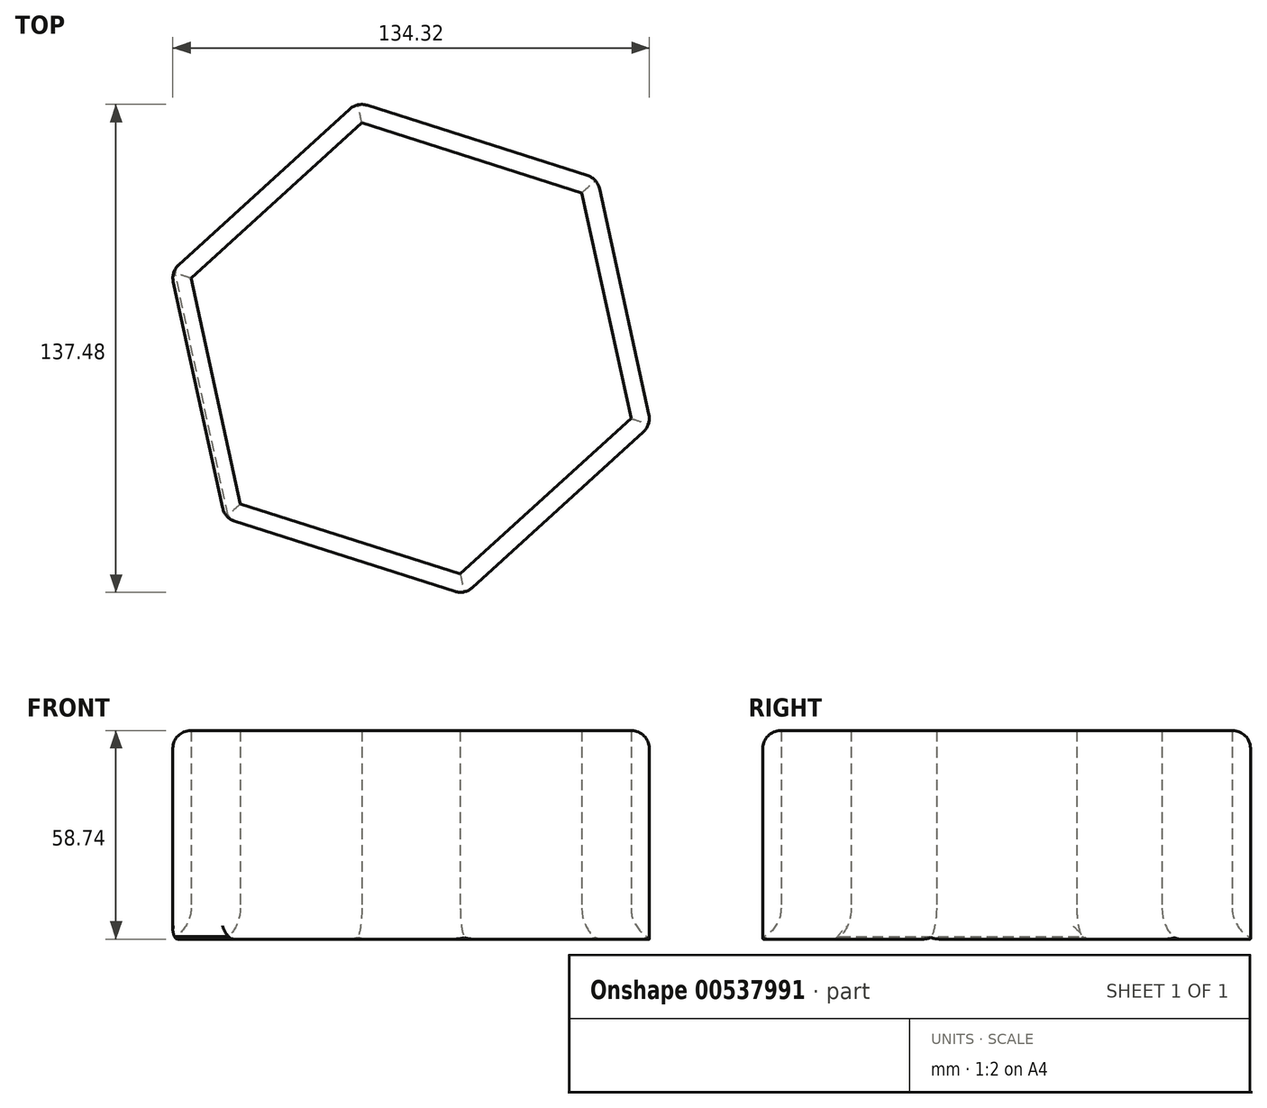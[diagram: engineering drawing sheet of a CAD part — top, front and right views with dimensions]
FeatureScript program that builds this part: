
annotation { "Feature Type Name" : "Feature", "Feature Type Description" : "" }
export const myFeature = defineFeature(function(context is Context, id is Id, definition is map)
    precondition{}
    {
        {
            var Q0;
            Q0=qCreatedBy(makeId("Top.planeOp"),FACE);
            var sketch = newSketch(context, id + "F0", { "sketchPlane" : qUnion([Q0])});
            skCircle(sketch, "E0.cCircle", {"center": v(0, 0) * mm, "radius": 61.5 * mm, "construction": true});
            skLineSegment(sketch, "E0.0", {"start": v(67.66, -21.57) * mm, "end": v(15.15, -69.38) * mm});
            skLineSegment(sketch, "E0.1", {"start": v(15.15, -69.38) * mm, "end": v(-52.51, -47.8) * mm});
            skLineSegment(sketch, "E0.2", {"start": v(-52.51, -47.8) * mm, "end": v(-67.66, 21.57) * mm});
            skLineSegment(sketch, "E0.3", {"start": v(-67.66, 21.57) * mm, "end": v(-15.15, 69.38) * mm});
            skLineSegment(sketch, "E0.4", {"start": v(-15.15, 69.38) * mm, "end": v(52.51, 47.8) * mm});
            skLineSegment(sketch, "E0.5", {"start": v(52.51, 47.8) * mm, "end": v(67.66, -21.57) * mm});
            skPoint(sketch, "E0.0.midPoint", {"position": v(41.4, -45.48) * mm});
            skCircle(sketch, "E1.cCircle", {"center": v(0, 0) * mm, "radius": 56.37 * mm, "construction": true});
            skLineSegment(sketch, "E1.0", {"start": v(62.01, -19.77) * mm, "end": v(13.88, -63.6) * mm});
            skLineSegment(sketch, "E1.1", {"start": v(13.88, -63.6) * mm, "end": v(-48.13, -43.82) * mm});
            skLineSegment(sketch, "E1.2", {"start": v(-48.13, -43.82) * mm, "end": v(-62.01, 19.77) * mm});
            skLineSegment(sketch, "E1.3", {"start": v(-62.01, 19.77) * mm, "end": v(-13.88, 63.6) * mm});
            skLineSegment(sketch, "E1.4", {"start": v(-13.88, 63.6) * mm, "end": v(48.13, 43.82) * mm});
            skLineSegment(sketch, "E1.5", {"start": v(48.13, 43.82) * mm, "end": v(62.01, -19.77) * mm});
            skPoint(sketch, "E1.0.midPoint", {"position": v(37.95, -41.68) * mm});
            skSolve(sketch);
        }
        {
            var Q0;
            Q0 = qSketchRegion(id + "F0", true);
            extrude(context, id + "F1", {"entities" : qUnion([Q0]), "depth" : 60 * mm, "offsetDistance" : 25 * mm});
        }
        {
            var Q0;
            Q0=makeQuery(id+"F1.opExtrude","SWEPT_EDGE",EDGE,{"disambiguationData":[OSD([sQuery(id+"F0.wireOp",EDGE,"E0.4"),sQuery(id+"F0.wireOp",EDGE,"E0.5")])]});
            var Q1;
            Q1=makeQuery(id+"F1.opExtrude","CAP_EDGE",EDGE,{"disambiguationData":[OSD([sQuery(id+"F0.wireOp",EDGE,"E0.5")])],"isStart":false});
            var Q2;
            Q2=makeQuery(id+"F1.opExtrude","CAP_EDGE",EDGE,{"disambiguationData":[OSD([sQuery(id+"F0.wireOp",EDGE,"E0.4")])],"isStart":false});
            var Q3;
            Q3=makeQuery(id+"F1.opExtrude","SWEPT_EDGE",EDGE,{"disambiguationData":[OSD([sQuery(id+"F0.wireOp",EDGE,"E0.3"),sQuery(id+"F0.wireOp",EDGE,"E0.4")])]});
            var Q4;
            Q4=makeQuery(id+"F1.opExtrude","CAP_EDGE",EDGE,{"disambiguationData":[OSD([sQuery(id+"F0.wireOp",EDGE,"E0.1")])],"isStart":false});
            var Q5;
            Q5=makeQuery(id+"F1.opExtrude","SWEPT_EDGE",EDGE,{"disambiguationData":[OSD([sQuery(id+"F0.wireOp",EDGE,"E0.0"),sQuery(id+"F0.wireOp",EDGE,"E0.1")])]});
            var Q6;
            Q6=makeQuery(id+"F1.opExtrude","SWEPT_EDGE",EDGE,{"disambiguationData":[OSD([sQuery(id+"F0.wireOp",EDGE,"E0.0"),sQuery(id+"F0.wireOp",EDGE,"E0.5")])]});
            var Q7;
            Q7=makeQuery(id+"F1.opExtrude","CAP_EDGE",EDGE,{"disambiguationData":[OSD([sQuery(id+"F0.wireOp",EDGE,"E0.0")])],"isStart":false});
            var Q8;
            Q8=makeQuery(id+"F1.opExtrude","SWEPT_EDGE",EDGE,{"disambiguationData":[OSD([sQuery(id+"F0.wireOp",EDGE,"E0.1"),sQuery(id+"F0.wireOp",EDGE,"E0.2")])]});
            var Q9;
            Q9=makeQuery(id+"F1.opExtrude","SWEPT_FACE",FACE,{"disambiguationData":[OSD([sQuery(id+"F0.wireOp",EDGE,"E0.2")])]});
            var Q10;
            Q10=makeQuery(id+"F1.opExtrude","CAP_EDGE",EDGE,{"disambiguationData":[OSD([sQuery(id+"F0.wireOp",EDGE,"E0.3")])],"isStart":false});
            fillet(context, id + "F2", {"entities" : qUnion([Q0, Q1, Q2, Q3, Q4, Q5, Q6, Q7, Q8, Q9, Q10]), "radius" : 5 * mm, "tangentPropagation" : true, "allowEdgeOverflow" : false});
        }
        {
            var Q0;
            Q0=makeQuery(id+"F1.opExtrude","CAP_EDGE",EDGE,{"disambiguationData":[OSD([sQuery(id+"F0.wireOp",EDGE,"E1.4")])],"isStart":true});
            var Q1;
            Q1=makeQuery(id+"F1.opExtrude","CAP_EDGE",EDGE,{"disambiguationData":[OSD([sQuery(id+"F0.wireOp",EDGE,"E1.3")])],"isStart":true});
            var Q2;
            Q2=makeQuery(id+"F1.opExtrude","CAP_EDGE",EDGE,{"disambiguationData":[OSD([sQuery(id+"F0.wireOp",EDGE,"E1.2")])],"isStart":true});
            var Q3;
            Q3=makeQuery(id+"F1.opExtrude","CAP_EDGE",EDGE,{"disambiguationData":[OSD([sQuery(id+"F0.wireOp",EDGE,"E1.1")])],"isStart":true});
            var Q4;
            Q4=makeQuery(id+"F1.opExtrude","CAP_EDGE",EDGE,{"disambiguationData":[OSD([sQuery(id+"F0.wireOp",EDGE,"E1.5")])],"isStart":true});
            var Q5;
            Q5=makeQuery(id+"F1.opExtrude","CAP_EDGE",EDGE,{"disambiguationData":[OSD([sQuery(id+"F0.wireOp",EDGE,"E1.0")])],"isStart":true});
            fillet(context, id + "F3", {"entities" : qUnion([Q0, Q1, Q2, Q3, Q4, Q5]), "radius" : 10 * mm, "tangentPropagation" : true, "allowEdgeOverflow" : false});
        }
    });
